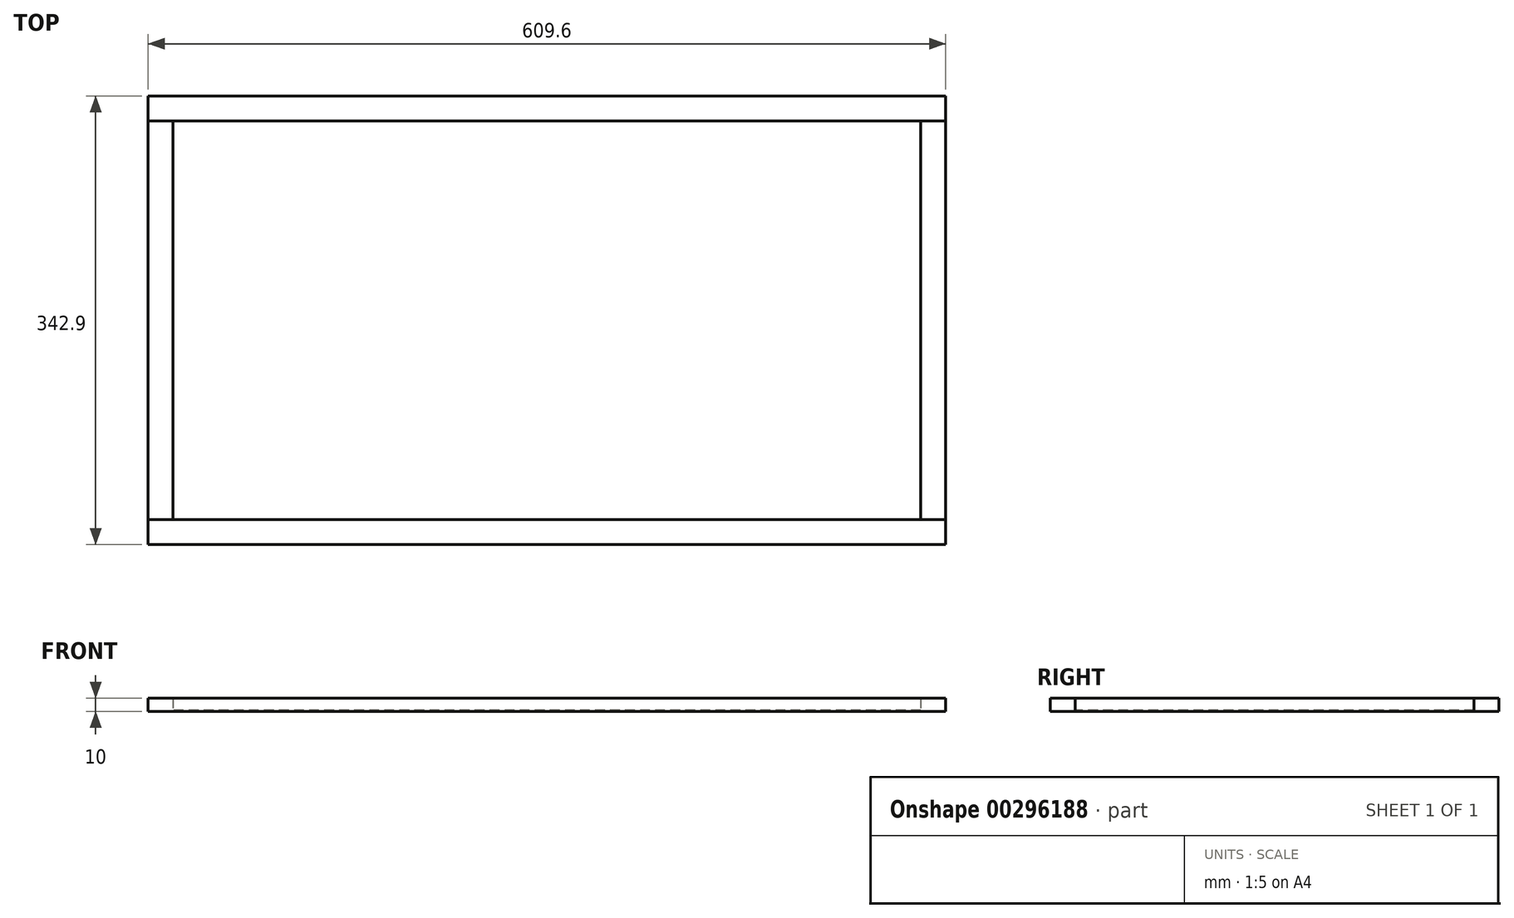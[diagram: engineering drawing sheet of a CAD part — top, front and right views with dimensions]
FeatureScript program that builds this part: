
annotation { "Feature Type Name" : "Feature", "Feature Type Description" : "" }
export const myFeature = defineFeature(function(context is Context, id is Id, definition is map)
    precondition{}
    {
        {
            assignVariable(context, id + "F0", {"name" : "bt", "anyValue" : 0.75});
        }
        {
            assignVariable(context, id + "F1", {"name" : "plht", "anyValue" : 10});
        }
        {
            var Q0;
            Q0=qCreatedBy(makeId("Top.planeOp"),FACE);
            var sketch = newSketch(context, id + "F2", { "sketchPlane" : qUnion([Q0])});
            skLineSegment(sketch, "E0.bottom", {"start": v(285.75, 152.4) * mm, "end": v(-285.75, 152.4) * mm});
            skLineSegment(sketch, "E0.top", {"start": v(285.75, -152.4) * mm, "end": v(-285.75, -152.4) * mm});
            skLineSegment(sketch, "E0.left", {"start": v(285.75, 152.4) * mm, "end": v(285.75, -152.4) * mm});
            skLineSegment(sketch, "E0.right", {"start": v(-285.75, 152.4) * mm, "end": v(-285.75, -152.4) * mm});
            skPoint(sketch, "E0.middle", {"position": v(0, 0) * mm});
            skLineSegment(sketch, "E1.bottom", {"start": v(285.75, 152.4) * mm, "end": v(304.8, 152.4) * mm});
            skLineSegment(sketch, "E1.top", {"start": v(285.75, -152.4) * mm, "end": v(304.8, -152.4) * mm});
            skLineSegment(sketch, "E1.right", {"start": v(304.8, 152.4) * mm, "end": v(304.8, -152.4) * mm});
            skLineSegment(sketch, "E2.bottom", {"start": v(-285.75, 152.4) * mm, "end": v(-304.8, 152.4) * mm});
            skLineSegment(sketch, "E2.top", {"start": v(-285.75, -152.4) * mm, "end": v(-304.8, -152.4) * mm});
            skLineSegment(sketch, "E2.right", {"start": v(-304.8, 152.4) * mm, "end": v(-304.8, -152.4) * mm});
            skLineSegment(sketch, "E3.bottom", {"start": v(-304.8, -152.4) * mm, "end": v(304.8, -152.4) * mm});
            skLineSegment(sketch, "E3.top", {"start": v(-304.8, -171.45) * mm, "end": v(304.8, -171.45) * mm});
            skLineSegment(sketch, "E3.left", {"start": v(-304.8, -152.4) * mm, "end": v(-304.8, -171.45) * mm});
            skLineSegment(sketch, "E3.right", {"start": v(304.8, -152.4) * mm, "end": v(304.8, -171.45) * mm});
            skPoint(sketch, "E4.middle", {"position": v(-304.8, 152.4) * mm});
            skLineSegment(sketch, "E5.bottom", {"start": v(-304.8, 152.4) * mm, "end": v(304.8, 152.4) * mm});
            skLineSegment(sketch, "E5.top", {"start": v(-304.8, 171.45) * mm, "end": v(304.8, 171.45) * mm});
            skLineSegment(sketch, "E5.left", {"start": v(-304.8, 152.4) * mm, "end": v(-304.8, 171.45) * mm});
            skLineSegment(sketch, "E5.right", {"start": v(304.8, 152.4) * mm, "end": v(304.8, 171.45) * mm});
            skSolve(sketch);
        }
        {
            var Q0;
            {var subQ0=sQuery(id+"F2.wireOp",EDGE,"E0.left");Q0=makeQuery(id+"F2.imprint","IMPRINT",FACE,{"disambiguationData":[TD([[makeQuery(id+"F2.imprint","IMPRINT",EDGE,{"derivedFrom":subQ0}),-1.0]])]});}
            extrude(context, id + "F3", {"entities" : qUnion([Q0]), "depth" : (getVariable(context, 'bt')) * mm});
        }
        {
            var Q0;
            {var subQ0=sQuery(id+"F2.wireOp",EDGE,"E0.right");Q0=makeQuery(id+"F2.imprint","IMPRINT",FACE,{"disambiguationData":[TD([[makeQuery(id+"F2.imprint","IMPRINT",EDGE,{"derivedFrom":subQ0}),-1.0]])]});}
            var Q1;
            {var subQ0=sQuery(id+"F2.wireOp",EDGE,"E0.left");Q1=makeQuery(id+"F2.imprint","IMPRINT",FACE,{"disambiguationData":[TD([[makeQuery(id+"F2.imprint","IMPRINT",EDGE,{"derivedFrom":subQ0}),1.0]])]});}
            extrude(context, id + "F4", {"entities" : qUnion([Q0, Q1]), "depth" : (getVariable(context, 'plht')) * mm});
        }
        {
            var Q0;
            Q0=makeQuery(id+"F2.imprint","IMPRINT",FACE,{"disambiguationData":[TD([[makeQuery(id+"F2.imprint","IMPRINT",EDGE,{"derivedFrom":sQuery(id+"F2.wireOp",EDGE,"E3.top")}),1.0]])]});
            var Q1;
            Q1=makeQuery(id+"F2.imprint","IMPRINT",FACE,{"disambiguationData":[TD([[makeQuery(id+"F2.imprint","IMPRINT",EDGE,{"derivedFrom":sQuery(id+"F2.wireOp",EDGE,"E5.top")}),-1.0]])]});
            extrude(context, id + "F5", {"entities" : qUnion([Q0, Q1]), "depth" : (getVariable(context, 'plht')) * mm});
        }
    });
